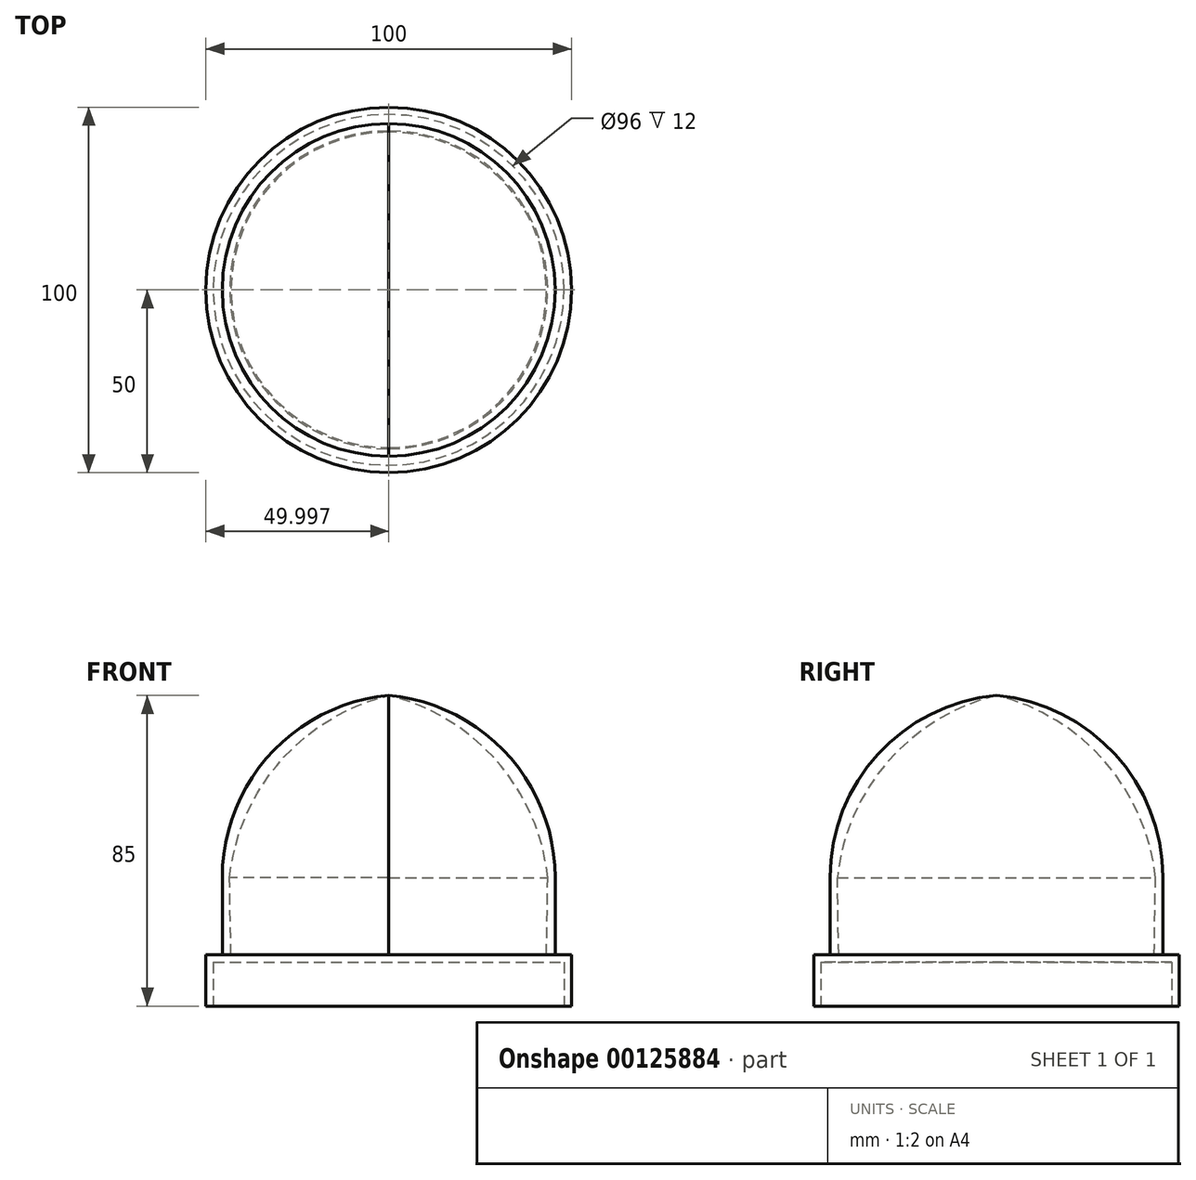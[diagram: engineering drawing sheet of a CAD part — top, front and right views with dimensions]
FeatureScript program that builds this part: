
annotation { "Feature Type Name" : "Feature", "Feature Type Description" : "" }
export const myFeature = defineFeature(function(context is Context, id is Id, definition is map)
    precondition{}
    {
        {
            var Q0;
            Q0=qCreatedBy(makeId("Front.planeOp"),FACE);
            var sketch = newSketch(context, id + "F0", { "sketchPlane" : qUnion([Q0])});
            skLineSegment(sketch, "E0", {"start": v(-86.87, -4.8) * mm, "end": v(-86.87, -26) * mm});
            skArc(sketch, "E1.filletArc", {"start": v(-41.34, 45) * mm, "mid": v(-73.77, 28.93) * mm, "end": v(-86.87, -4.8) * mm});
            skLineSegment(sketch, "E2", {"start": v(-41.34, 45) * mm, "end": v(-41.34, -40) * mm, "construction": true});
            skArc(sketch, "E3", {"start": v(-41.34, 45) * mm, "mid": v(-71.01, 26.94) * mm, "end": v(-84.87, -4.92) * mm});
            skLineSegment(sketch, "E4", {"start": v(-84.5, -26) * mm, "end": v(-84.87, -4.92) * mm});
            skPoint(sketch, "E5.visualSharp", {"position": v(-34.87, 108.2) * mm});
            skLineSegment(sketch, "E6.MirrorCS", {"start": v(1.82, -26) * mm, "end": v(2.19, -4.92) * mm});
            skArc(sketch, "E7.MirrorCS", {"start": v(-41.34, 45) * mm, "mid": v(-8.91, 28.93) * mm, "end": v(4.18, -4.8) * mm});
            skLineSegment(sketch, "E8.MirrorCS", {"start": v(4.18, -4.8) * mm, "end": v(4.18, -26) * mm});
            skArc(sketch, "E9.MirrorCS", {"start": v(-41.34, 45) * mm, "mid": v(-11.67, 26.94) * mm, "end": v(2.19, -4.92) * mm});
            skLineSegment(sketch, "E10", {"start": v(4.18, -26) * mm, "end": v(-41.34, -26) * mm});
            skLineSegment(sketch, "E11", {"start": v(-41.34, -26) * mm, "end": v(-41.34, 45) * mm});
            skLineSegment(sketch, "E12", {"start": v(-41.34, -40) * mm, "end": v(-41.34, -26) * mm});
            skLineSegment(sketch, "E13", {"start": v(-91.34, -40) * mm, "end": v(-41.34, -40) * mm});
            skLineSegment(sketch, "E14", {"start": v(-41.34, -26) * mm, "end": v(-91.34, -26) * mm});
            skLineSegment(sketch, "E15", {"start": v(-91.34, -26) * mm, "end": v(-91.34, -40) * mm});
            skSolve(sketch);
        }
        {
            var Q0;
            {var subQ3=sQuery(id+"F0.wireOp",EDGE,"E12");Q0=makeQuery(id+"F0.imprint","IMPRINT",FACE,{"disambiguationData":[TD([[makeQuery(id+"F0.imprint","IMPRINT",EDGE,{"derivedFrom":subQ3}),1.0]])]});}
            var Q1;
            Q1=sQuery(id+"F0.wireOp",EDGE,"E12");
            revolve(context, id + "F1", {"entities" : qUnion([Q0]), "axis" : qUnion([Q1]), "revolveType" : RevolveType.FULL});
        }
        {
            var Q0;
            {var subQ0=sQuery(id+"F0.wireOp",EDGE,"E0");Q0=makeQuery(id+"F0.imprint","IMPRINT",FACE,{"disambiguationData":[TD([[makeQuery(id+"F0.imprint","IMPRINT",EDGE,{"derivedFrom":subQ0}),1.0]])]});}
            var Q1;
            Q1=sQuery(id+"F0.wireOp",EDGE,"E2");
            revolve(context, id + "F2", {"operationType" : NewBodyOperationType.ADD, "entities" : qUnion([Q0]), "axis" : qUnion([Q1]), "revolveType" : RevolveType.SYMMETRIC, "angle" : 180 * degree});
        }
        {
            var Q0;
            {var subQ1=sQuery(id+"F0.wireOp",EDGE,"E6.MirrorCS");Q0=makeQuery(id+"F0.imprint","IMPRINT",FACE,{"disambiguationData":[TD([[makeQuery(id+"F0.imprint","IMPRINT",EDGE,{"derivedFrom":subQ1}),-1.0]])]});}
            var Q1;
            Q1=sQuery(id+"F0.wireOp",EDGE,"E11");
            revolve(context, id + "F3", {"entities" : qUnion([Q0]), "axis" : qUnion([Q1]), "revolveType" : RevolveType.SYMMETRIC, "oppositeDirection" : true, "angle" : 180 * degree});
        }
        {
            var Q0;
            Q0=makeQuery(id+"F1.opRevolve","SWEPT_FACE",FACE,{"disambiguationData":[OSD([sQuery(id+"F0.wireOp",EDGE,"E13")])]});
            var sketch = newSketch(context, id + "F4", { "sketchPlane" : qUnion([Q0])});
            skCircle(sketch, "E16", {"center": v(-41.34, 0) * mm, "radius": 48 * mm});
            skSolve(sketch);
        }
        {
            var Q0;
            Q0 = qSketchRegion(id + "F4", true);
            extrude(context, id + "F5", {"entities" : qUnion([Q0]), "operationType" : NewBodyOperationType.REMOVE, "oppositeDirection" : true, "depth" : 12 * mm});
        }
    });
